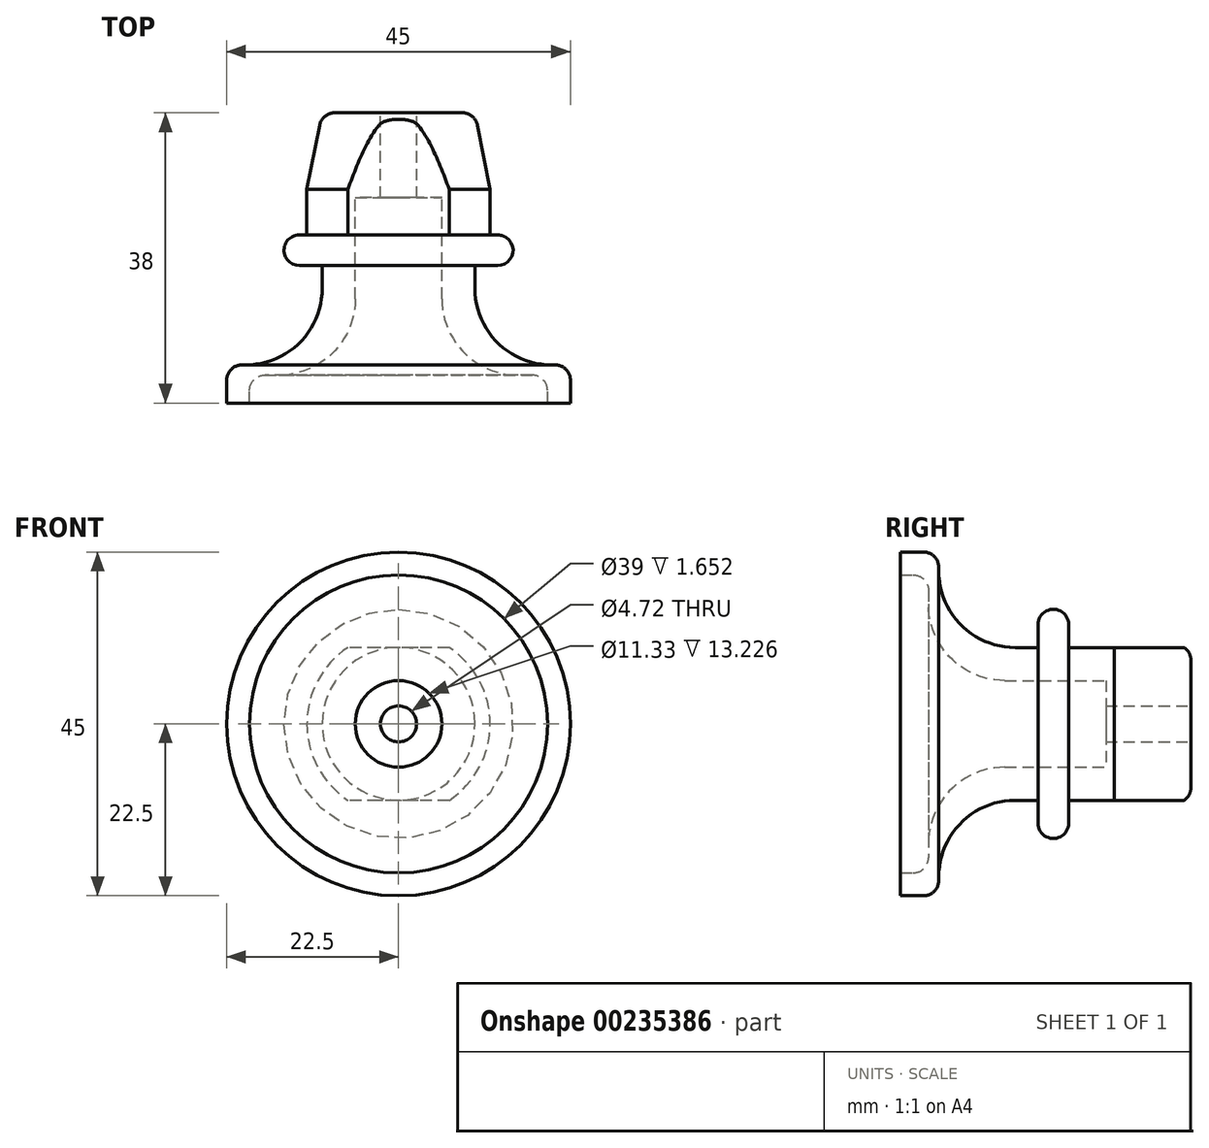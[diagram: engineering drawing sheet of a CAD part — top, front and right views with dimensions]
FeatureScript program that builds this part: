
annotation { "Feature Type Name" : "Feature", "Feature Type Description" : "" }
export const myFeature = defineFeature(function(context is Context, id is Id, definition is map)
    precondition{}
    {
        {
            var Q0;
            Q0=qCreatedBy(makeId("Top.planeOp"),FACE);
            var sketch = newSketch(context, id + "F0", { "sketchPlane" : qUnion([Q0])});
            skLineSegment(sketch, "E0", {"start": v(18.63, 0) * mm, "end": v(22.5, 0) * mm});
            skLineSegment(sketch, "E1", {"start": v(22.5, 0) * mm, "end": v(22.5, 3) * mm});
            skLineSegment(sketch, "E2", {"start": v(20.5, 5) * mm, "end": v(20, 5) * mm});
            skLineSegment(sketch, "E3", {"start": v(10, 15) * mm, "end": v(10, 18) * mm});
            skLineSegment(sketch, "E4", {"start": v(10, 18) * mm, "end": v(13, 18) * mm});
            skLineSegment(sketch, "E5", {"start": v(15, 20) * mm, "end": v(15, 20) * mm});
            skLineSegment(sketch, "E6", {"start": v(13, 22) * mm, "end": v(12, 22) * mm});
            skLineSegment(sketch, "E7", {"start": v(12, 22) * mm, "end": v(12, 28) * mm});
            skLineSegment(sketch, "E8", {"start": v(12, 28) * mm, "end": v(10.32, 36.4) * mm});
            skLineSegment(sketch, "E9", {"start": v(8.36, 38) * mm, "end": v(2.36, 38) * mm});
            skPoint(sketch, "E10.visualSharp", {"position": v(22.5, 5) * mm});
            skArc(sketch, "E10.filletArc", {"start": v(22.5, 3) * mm, "mid": v(21.91, 4.41) * mm, "end": v(20.5, 5) * mm});
            skPoint(sketch, "E11.visualSharp", {"position": v(15, 18) * mm});
            skArc(sketch, "E11.filletArc", {"start": v(13, 18) * mm, "mid": v(14.41, 18.59) * mm, "end": v(15, 20) * mm});
            skPoint(sketch, "E12.visualSharp", {"position": v(15, 22) * mm});
            skArc(sketch, "E12.filletArc", {"start": v(15, 20) * mm, "mid": v(14.41, 21.41) * mm, "end": v(13, 22) * mm});
            skPoint(sketch, "E13.visualSharp", {"position": v(10, 5) * mm});
            skArc(sketch, "E13.filletArc", {"start": v(10, 15) * mm, "mid": v(12.93, 7.93) * mm, "end": v(20, 5) * mm});
            skLineSegment(sketch, "E14", {"start": v(2.36, 38) * mm, "end": v(2.36, 26.88) * mm});
            skLineSegment(sketch, "E15", {"start": v(2.36, 26.88) * mm, "end": v(5.67, 26.88) * mm});
            skLineSegment(sketch, "E16", {"start": v(5.67, 26.88) * mm, "end": v(5.67, 13.65) * mm});
            skLineSegment(sketch, "E17", {"start": v(15.67, 3.65) * mm, "end": v(17.5, 3.65) * mm});
            skLineSegment(sketch, "E18", {"start": v(19.5, 1.65) * mm, "end": v(19.5, 0) * mm});
            skPoint(sketch, "E19.visualSharp", {"position": v(5.67, 3.65) * mm});
            skArc(sketch, "E19.filletArc", {"start": v(5.67, 13.65) * mm, "mid": v(8.6, 6.58) * mm, "end": v(15.67, 3.65) * mm});
            skPoint(sketch, "E20.visualSharp", {"position": v(19.5, 3.65) * mm});
            skArc(sketch, "E20.filletArc", {"start": v(19.5, 1.65) * mm, "mid": v(18.91, 3.07) * mm, "end": v(17.5, 3.65) * mm});
            skPoint(sketch, "E21.orphan", {"position": v(0, 38) * mm});
            skPoint(sketch, "E22.visualSharp", {"position": v(10, 38) * mm});
            skArc(sketch, "E22.filletArc", {"start": v(10.32, 36.4) * mm, "mid": v(9.63, 37.55) * mm, "end": v(8.36, 38) * mm});
            skLineSegment(sketch, "E23", {"start": v(0, 45.21) * mm, "end": v(0, -5.44) * mm, "construction": true});
            skSolve(sketch);
        }
        {
            var Q0;
            {var subQ0=sQuery(id+"F0.wireOp",EDGE,"E1");Q0=makeQuery(id+"F0.imprint","IMPRINT",FACE,{"disambiguationData":[TD([[makeQuery(id+"F0.imprint","IMPRINT",EDGE,{"derivedFrom":subQ0}),1.0]])]});}
            var Q1;
            Q1=sQuery(id+"F0.wireOp",EDGE,"E23");
            revolve(context, id + "F1", {"entities" : qUnion([Q0]), "axis" : qUnion([Q1]), "revolveType" : RevolveType.FULL});
        }
        {
            var Q0;
            Q0=makeQuery(id+"F1.opRevolve","SWEPT_FACE",FACE,{"disambiguationData":[OSD([sQuery(id+"F0.wireOp",EDGE,"E6")])]});
            var sketch = newSketch(context, id + "F2", { "sketchPlane" : qUnion([Q0])});
            skCircle(sketch, "E24.0", {"center": v(0, 0) * mm, "radius": 12 * mm, "construction": true});
            skLineSegment(sketch, "E25.bottom", {"start": v(-6.63, 10) * mm, "end": v(6.63, 10) * mm});
            skLineSegment(sketch, "E25.top", {"start": v(-6.63, -10) * mm, "end": v(6.63, -10) * mm});
            skLineSegment(sketch, "E25.left", {"start": v(-6.63, 10) * mm, "end": v(-6.63, -10) * mm});
            skLineSegment(sketch, "E25.right", {"start": v(6.63, 10) * mm, "end": v(6.63, -10) * mm});
            skCircle(sketch, "E26", {"center": v(0, 0) * mm, "radius": 12 * mm});
            skSolve(sketch);
        }
        {
            var Q0;
            {var subQ0=sQuery(id+"F2.wireOp",EDGE,"E25.bottom");Q0=makeQuery(id+"F2.imprint","IMPRINT",FACE,{"disambiguationData":[TD([[makeQuery(id+"F2.imprint","IMPRINT",EDGE,{"derivedFrom":subQ0}),1.0]])]});}
            var Q1;
            {var subQ0=sQuery(id+"F2.wireOp",EDGE,"E25.top");Q1=makeQuery(id+"F2.imprint","IMPRINT",FACE,{"disambiguationData":[TD([[makeQuery(id+"F2.imprint","IMPRINT",EDGE,{"derivedFrom":subQ0}),-1.0]])]});}
            extrude(context, id + "F3", {"entities" : qUnion([Q0, Q1]), "operationType" : NewBodyOperationType.REMOVE, "depth" : 25 * mm});
        }
    });
